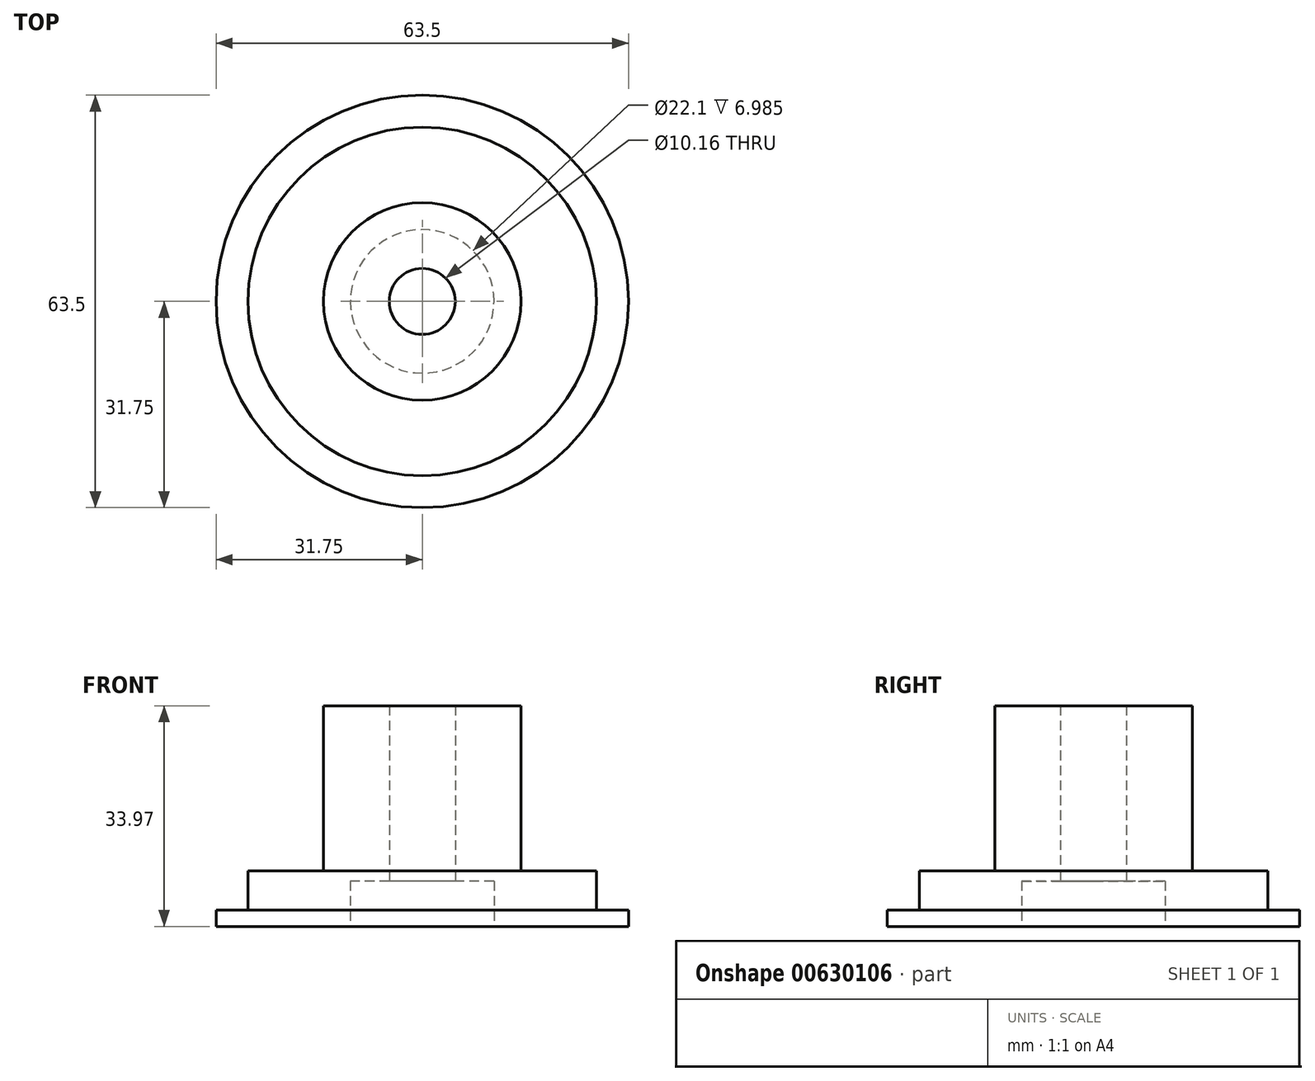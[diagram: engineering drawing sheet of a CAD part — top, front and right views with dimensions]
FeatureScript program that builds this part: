
annotation { "Feature Type Name" : "Feature", "Feature Type Description" : "" }
export const myFeature = defineFeature(function(context is Context, id is Id, definition is map)
    precondition{}
    {
        {
            var Q0;
            Q0=qCreatedBy(makeId("Top.planeOp"),FACE);
            var sketch = newSketch(context, id + "F0", { "sketchPlane" : qUnion([Q0])});
            skCircle(sketch, "E0", {"center": v(0, 0) * mm, "radius": 11.05 * mm});
            skCircle(sketch, "E1", {"center": v(0, 0) * mm, "radius": 26.82 * mm});
            skCircle(sketch, "E2", {"center": v(0, 0) * mm, "radius": 31.75 * mm});
            skSolve(sketch);
        }
        {
            var Q0;
            Q0=makeQuery(id+"F0.imprint","IMPRINT",FACE,{"disambiguationData":[TD([[makeQuery(id+"F0.imprint","IMPRINT",EDGE,{"derivedFrom":sQuery(id+"F0.wireOp",EDGE,"E0")}),-1.0]])]});
            extrude(context, id + "F1", {"entities" : qUnion([Q0]), "depth" : 7 * mm, "offsetDistance" : 25.4 * mm});
        }
        {
            var Q0;
            Q0 = qSketchRegion(id + "F0", true);
            extrude(context, id + "F2", {"entities" : qUnion([Q0]), "operationType" : NewBodyOperationType.ADD, "depth" : 2.54 * mm, "offsetDistance" : 25.4 * mm});
        }
        {
            var Q0;
            Q0=makeQuery(id+"F1.opExtrude","CAP_FACE",FACE,{"disambiguationData":[OSD([sQuery(id+"F0.wireOp",EDGE,"E0"),sQuery(id+"F0.wireOp",EDGE,"E1")])],"isStart":false});
            var sketch = newSketch(context, id + "F3", { "sketchPlane" : qUnion([Q0])});
            skCircle(sketch, "E3", {"center": v(0, 0) * mm, "radius": 5.08 * mm});
            skCircle(sketch, "E4", {"center": v(0, 0) * mm, "radius": 26.82 * mm});
            skSolve(sketch);
        }
        {
            var Q0;
            Q0=makeQuery(id+"F3.imprint","IMPRINT",FACE,{"disambiguationData":[TD([[makeQuery(id+"F3.imprint","IMPRINT",EDGE,{"derivedFrom":sQuery(id+"F3.wireOp",EDGE,"E4")}),1.0]])]});
            var Q1;
            Q1=makeQuery(id+"F3.imprint","IMPRINT",FACE,{"disambiguationData":[TD([[makeQuery(id+"F3.imprint","IMPRINT",EDGE,{"derivedFrom":sQuery(id+"F3.wireOp",EDGE,"E3")}),-1.0]])]});
            extrude(context, id + "F4", {"entities" : qUnion([Q0, Q1]), "operationType" : NewBodyOperationType.ADD, "depth" : 1.59 * mm, "offsetDistance" : 25.4 * mm});
        }
        {
            var Q0;
            Q0=makeQuery(id+"F4.opExtrude","CAP_FACE",FACE,{"disambiguationData":[OSD([sQuery(id+"F3.wireOp",EDGE,"E3"),sQuery(id+"F3.wireOp",EDGE,"E4")])],"isStart":false});
            var sketch = newSketch(context, id + "F5", { "sketchPlane" : qUnion([Q0])});
            skCircle(sketch, "E5", {"center": v(0, 0) * mm, "radius": 15.2 * mm});
            skSolve(sketch);
        }
        {
            var Q0;
            Q0=makeQuery(id+"F5.imprint","IMPRINT",FACE,{"disambiguationData":[TD([[makeQuery(id+"F5.imprint","IMPRINT",EDGE,{"derivedFrom":sQuery(id+"F5.wireOp",EDGE,"E5")}),1.0]])]});
            extrude(context, id + "F6", {"entities" : qUnion([Q0]), "operationType" : NewBodyOperationType.ADD, "depth" : 25.4 * mm, "offsetDistance" : 25.4 * mm});
        }
    });
